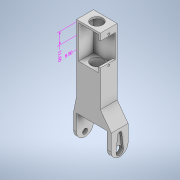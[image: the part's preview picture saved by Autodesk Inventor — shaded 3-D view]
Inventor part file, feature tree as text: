
AUTODESK INVENTOR PART (.ipt)
format: ipt  version: 2022.1 (Build 261234000, 234)  size: 257,536 bytes
history: native  units: mm
features: extrude x13, sketch x13, other x3, fillet x1
ambient origin geometry x8: Origin, YZ Plane, XZ Plane, XY Plane, X Axis, Y Axis, Z Axis, Center Point
bodies: Solid1 (feature_tree)
feature tree (30):
  other  "Annotations"
  extrude  "Extrusion1"  Depth=80.0mm
  extrude  "Extrusion2"  Depth=2.0mm
  extrude  "Extrusion3"  Depth=15.0mm TaperAngle=0.0deg
  extrude  "Extrusion4"  Depth=2.0mm
  extrude  "Extrusion5"  Depth=8.5mm
  extrude  "Extrusion9"  Depth=3.0mm
  extrude  "Extrusion10"  Depth=15.0mm
  extrude  "Extrusion11"  Depth=2.0mm
  extrude  "Extrusion12"  Depth=15.0mm TaperAngle=0.0deg
  extrude  "Extrusion13"  Depth=5.0mm TaperAngle=0.0deg
  extrude  "Extrusion14"  TaperAngle=0.0deg  [1 undecoded]
  fillet  "Fillet2"  Radius=3.0mm
  extrude  "Extrusion15"  TaperAngle=0.0deg  [1 undecoded]
  extrude  "Extrusion16"  Depth=4.0mm
  sketch  "Sketch1"  dims[d0=24.0mm d1=80.0mm]
  sketch  "Sketch2"  dims[d2=2.0mm d3=0.0mm d4=2.0mm]
  sketch  "Sketch3"  dims[d5=2.0mm d6=15.0mm d7=0.0mm]
  sketch  "Sketch4"  dims[d8=2.0mm d9=2.0mm]
  sketch  "Sketch5"  dims[d10=8.5mm d11=8.5mm]
  sketch  "Sketch12"  dims[d12=27.5mm d13=3.0mm]
  sketch  "Sketch13"  dims[d14=12.0mm d15=0.0mm d23=15.0mm]
  sketch  "Sketch14"  dims[d24=23.5mm d25=2.0mm]
  sketch  "Sketch15"  dims[d26=2.0mm d27=15.0mm d28=0.0mm]
  sketch  "Sketch16"  dims[d29=5.0mm d30=5.0mm d31=0.0mm]
  sketch  "Sketch17"  dims[d32=8.6mm d33=0.0mm d52=3.0mm]
  sketch  "Sketch18"  dims[d53=25.0mm d54=0.0mm]
  sketch  "Sketch20"  dims[d55=3.0mm d56=4.0mm d57=10.0mm d58=0.0mm d59=15.0mm d60=90.0deg d61=10.0mm d62=0.0mm d63=15.0mm d64=90.0deg d65=5.0mm d66=8.5mm d67=20.0mm d68=20.0mm d69=0.0mm d70=2.0mm d71=0.0mm d72=46.5mm d73=0.0mm d74=12.0mm d75=12.0mm d76=8.5mm d77=46.5mm d78=0.0mm d79=8.5mm d80=7.5mm d81=10.0mm d82=0.0mm d83=31.0mm d84=4.0mm d85=15.0mm d86=0.0mm d87=2.0mm d88=0.0mm d89=4.0mm d90=15.0mm d91=0.0mm d36=6.779666mm d37=11.6mm d43=1.279577mm d44=8.5mm]
  other  "Linear Dimension 1"
  other  "Linear Dimension 3"
note: 2 required parameter values undecoded (feature->parameter linkage not recoverable at this tier; creation-order binding heuristic only, values carry confidence <= 0.55)
